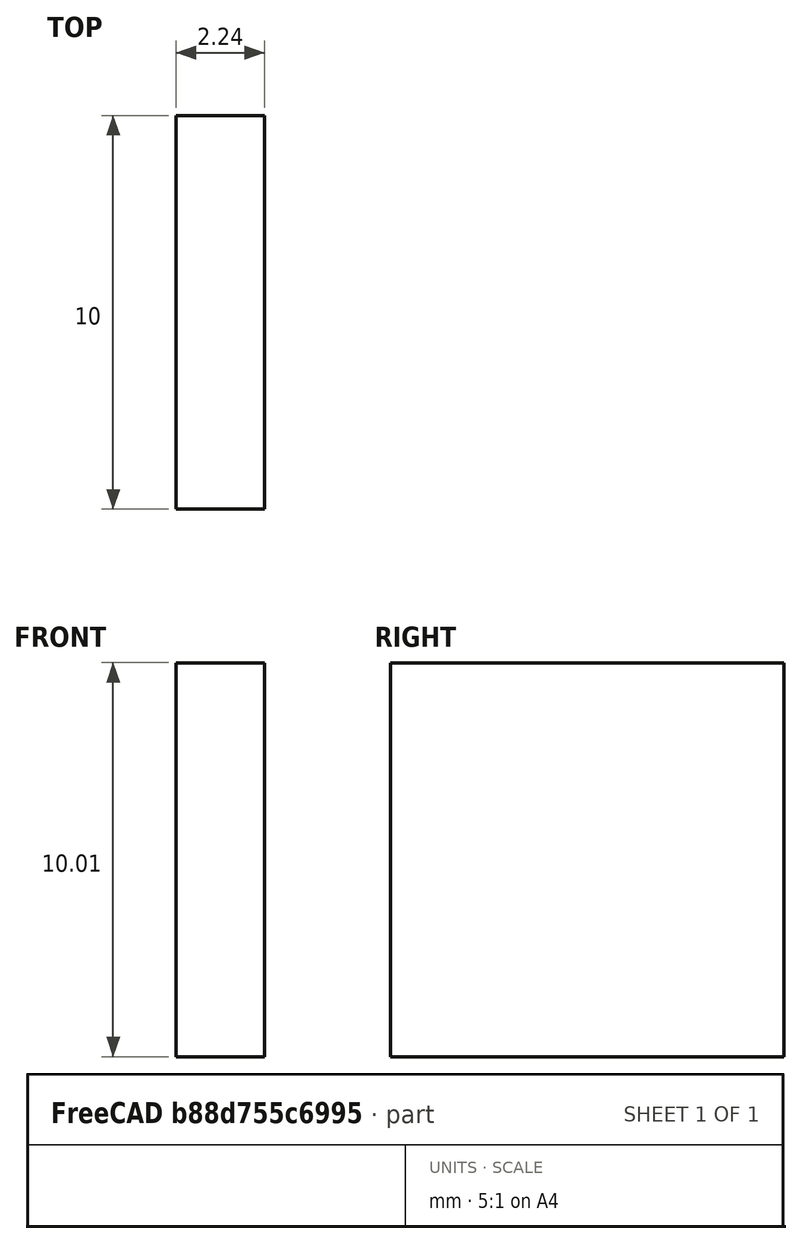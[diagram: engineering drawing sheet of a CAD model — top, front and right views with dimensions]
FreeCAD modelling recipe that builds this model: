
FCSTD DOCUMENT  (FreeCAD 0.19R24291 (Git))
Label: Seh2_wall_24
License: All rights reserved
LicenseURL: http://en.wikipedia.org/wiki/All_rights_reserved
objects: Sketcher::SketchObject×1, PartDesign::Pad×1, PartDesign::Body×1
note: 4 computed .brp shape members not serialized (recipe doc carries the construction recipe); baked Part::Feature solids carry a one-line shape summary decoded from their .brp

FEATURE [Sketcher::SketchObject] Sketch003
  FullyConstrained = false
  sketch-geometry (4):
    g0: LineSegment StartX=0 StartY=0 StartZ=0 EndX=2.24177 EndY=0 EndZ=0
    g1: LineSegment StartX=2.24177 StartY=0 StartZ=0 EndX=2.24177 EndY=10 EndZ=0
    g2: LineSegment StartX=2.24177 StartY=10 StartZ=0 EndX=0 EndY=10 EndZ=0
    g3: LineSegment StartX=0 StartY=10 StartZ=0 EndX=0 EndY=0 EndZ=0
  constraints (10):
    c: Coincident(g0,g1)
    c: Coincident(g1,g2)
    c: Coincident(g2,g3)
    c: Coincident(g3,g0)
    c: Horizontal(g0)
    c: Horizontal(g2)
    c: Vertical(g1)
    c: Vertical(g3)
    c: Coincident(g0,g-1)
    c: DistanceY(g0,g2) = 10
FEATURE [PartDesign::Pad] Pad
  Direction = (1,1,1)
  Length = 10.0076
  Length2 = 99.9998
  Profile = -> Sketch003
  Type = 0
FEATURE [PartDesign::Body] Body
  Group = -> [Sketch003,Pad]
  Origin = -> Origin
  Tip = -> Pad
